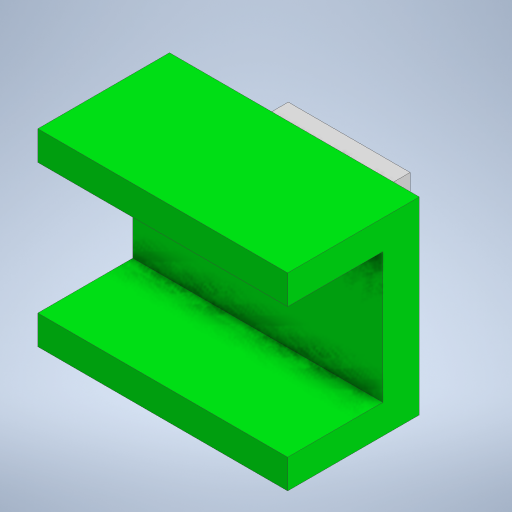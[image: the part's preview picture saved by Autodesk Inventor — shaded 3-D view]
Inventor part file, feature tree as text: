
AUTODESK INVENTOR PART (.ipt)
format: ipt  version: 2023 (Build 270158000, 158)  size: 241,152 bytes
history: native  units: mm
features: extrude x3, sketch x3, other x1
ambient origin geometry x8: Origin, YZ Plane, XZ Plane, XY Plane, X Axis, Y Axis, Z Axis, Center Point
bodies: Body1 (feature_tree)
feature tree (7):
  other  "솔리드1"
  extrude  "돌출1"  Depth=20.5mm
  extrude  "돌출2"  Depth=15.5mm
  extrude  "돌출3"  Depth=3.0mm TaperAngle=0.0deg
  sketch  "스케치1"
  sketch  "스케치2"
  sketch  "스케치3"
